# Revit family: Genelec_4435
name_source: partatom
category: Generic Models
units: mm (PartAtom-declared; Revit-internal decimal feet)

## family parameters
Always vertical = No
Can host rebar = No
Cut with Voids When Loaded = No
Maintain Annotation Orientation = No
Part Type = Normal
Room Calculation Point = Yes
Round Connector Dimension = Use Diameter
Shared = No
Work Plane-Based = Yes

## types (2) — shared parameters
Accuracy of Frequency Response = ± 2.5 dB (70 Hz - 20 kHz)
Acoustic Axis = 175
BIMobject category = Audio Electronics
Color = Genelec Black
Connections = 1 x RJ45 for PoE power, management and audio in AES67 / Dante format
1 x Euroblock Analog Input
Depth = 165 mm
Description = The 4435A Smart IP Active PoE-Powered In-ceiling Loudspeaker provides a discreet, durable and functional in-ceiling solution of the highest quality, with the added ease of installation, system scalability and simple operation of Smart IP's single-cable networked technology.
Dispersion Angle = H 120° V 100°
Driver Dimensions = ⌀ 130 mm Woofer + ⌀ 19 mm Tweeter
Export Type to IFC As = IfcAudioVisualApplianceType
Finish Type = Painted steel enclosure
Frequency Response = 58 Hz - 39 kHz (-6 dB)
Height = 165 mm
IFC Classification = Electric Appliance
IFC Name = 4435A
Line Drawing = https://assets.ctfassets.net
Mains Voltage = PoE+/PoE
Manufacturer = GENELEC
Manufacturer Country = Finland
Max. short term sine wave acoustic output  on axis in half space, averaged from 100Hz to 3 kHz = ≥ 104 dB SPL
Maximum long term RMS acoustic output in same conditions with IEC weighted noise (limited by driver unit protection circuit) = ≥ 96 dB SPL
Model = 4435
Model Description = Smart IP Active In-ceiling Loudspeaker
Model Image = https://images.ctfassets.net
Model Name = 4435A
Power Consumption = 26 W
Power consumption Idle = ≤5 W
Power consumption Standby = ≤4 W (ISS Active)
Price List Description = Closed-back in-ceiling installation loudspeaker with steel enclosure and simple latch fastening for easy installation and discreet low-profile magnetically attaching grille. Two drivers, woofer 130 mm (5 in) and tweeter 19 mm (3/4 in). Two Class D amplifiers 50 W + 50 W with integrated Smart IP crossover inside the loudspeaker. Maximum output 104 dB SPL, frequency response 58 Hz - 39 kHz (-6 dB). Connections: 1 x RJ45 (Dante/AES67, Smart IP Management, PoE power) interface and 1 x Euroblock analog input connector. Compatible with PoE+ (30W) and PoE (15W). API for automation systems. Setup by Smart IP Manager software, including device discovery, room equalisation, zone organisation and status monitoring. Integrated support point for safety wire (not included). Dimensions with round grille: Diam 288 mm x Depth 165 mm / Diam 11 3/8 in x Depth 6 1/2 in Dimensions with square grille: Length 288 mm x Width 288 mm x Depth 159 mm / Length 11 3/8 in x Width 11 3/8 in x Depth 6 1/4 in. Weight: 3.5 kg (7.7 lb)
Product Family = Installation Speaker
Product Group = 4000 Series Installation Speakers
Self-generated Noise = ≤5 dB
Type IFC Predefined Type = SPEAKER
Type Image = <None>
URL = https://www.genelec.com
Uniclass 2.0 Description = Sound Amplifiers
Weight = 3.5
Width = 288 mm  [stored 0.944882 ft]
zero-valued in all types: Default Elevation

## per-type parameters (varying)
| type | Square Grille |
| 4435 Round Grille | No |
| 4435 Square Grille | Yes |

note: [stored X ft] marks values corroborated as IEEE doubles in the binary element streams (Revit-internal decimal feet)
